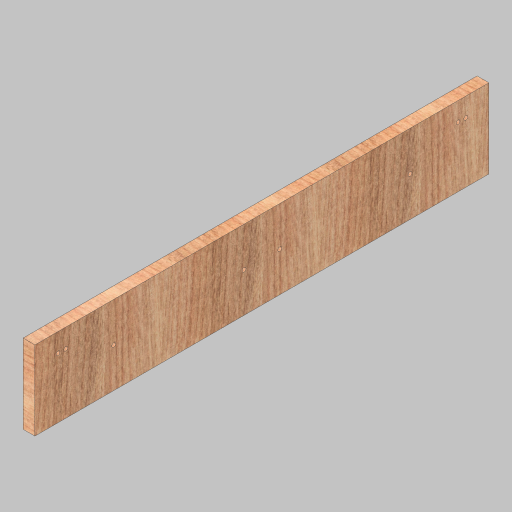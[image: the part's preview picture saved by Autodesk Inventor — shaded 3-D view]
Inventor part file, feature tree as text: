
AUTODESK INVENTOR PART (.ipt)
format: ipt  version: 2023.5 (Build 275446000, 446)  size: 240,640 bytes
history: native  units: in
note: dims shown in document units (in); Inventor stores cm internally (conversion verified against a paired STEP export)
features: sketch x3, hole x2, extrude x1
ambient origin geometry x8: Origin, YZ Plane, XZ Plane, XY Plane, X Axis, Y Axis, Z Axis, Center Point
bodies: Solid1 (feature_tree)
feature tree (6):
  extrude  "Extrusion1"  Depth=28.75in
  hole  "Hole1"  [1 undecoded]
  hole  "Hole2"  [1 undecoded]
  sketch  "Sketch1"  dims[d0=5.0in d1=28.75in]
  sketch  "Sketch2"  dims[d2=0.75in d3=0.0in d4=1.461in]
  sketch  "Sketch3"  dims[d5=0.5in d6=1.188in d7=0.25in d8=0.75in d9=0.385in d10=0.25in d11=0.5635in d12=1.0in d13=0.8108in d16=4.995in d17=8.25in d18=0.25in d19=0.75in d20=0.385in d21=0.25in d22=0.5635in d23=1.0in d24=0.8108in]
note: 2 required parameter values undecoded (feature->parameter linkage not recoverable at this tier; creation-order binding heuristic only, values carry confidence <= 0.55)
